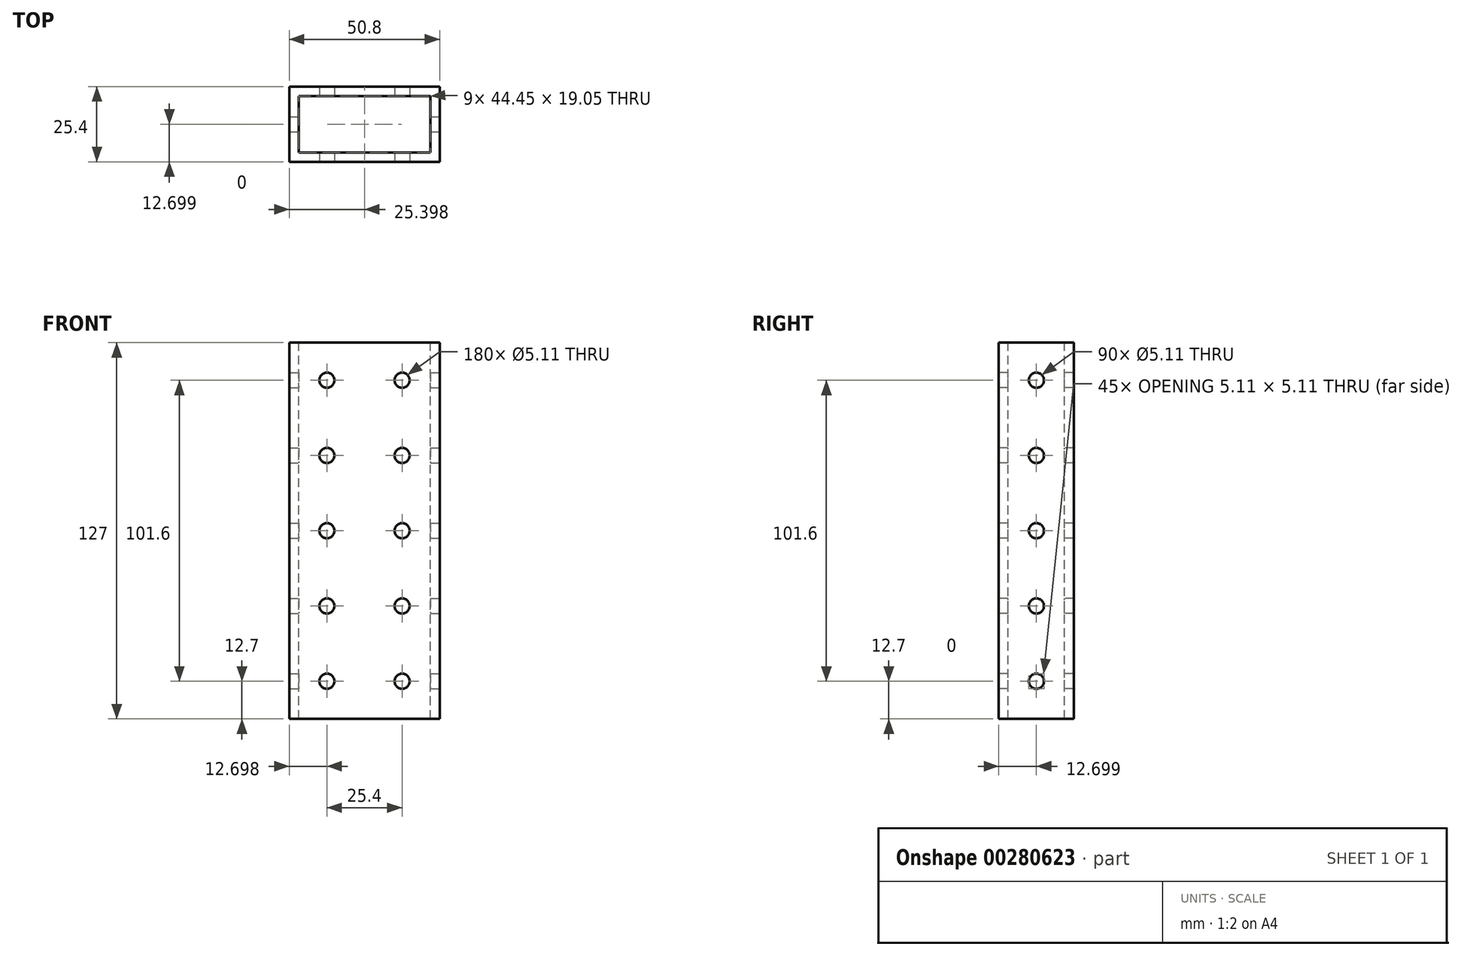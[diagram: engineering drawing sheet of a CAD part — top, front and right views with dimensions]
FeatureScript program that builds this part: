
annotation { "Feature Type Name" : "Feature", "Feature Type Description" : "" }
export const myFeature = defineFeature(function(context is Context, id is Id, definition is map)
    precondition{}
    {
        {
            var Q0;
            Q0=qCreatedBy(makeId("Top.planeOp"),FACE);
            var sketch = newSketch(context, id + "F0", { "sketchPlane" : qUnion([Q0])});
            skLineSegment(sketch, "E0.bottom", {"start": v(-19.05, 5.92) * mm, "end": v(31.75, 5.92) * mm});
            skLineSegment(sketch, "E0.top", {"start": v(-19.05, -19.48) * mm, "end": v(31.75, -19.48) * mm});
            skLineSegment(sketch, "E0.left", {"start": v(-19.05, 5.92) * mm, "end": v(-19.05, -19.48) * mm});
            skLineSegment(sketch, "E0.right", {"start": v(31.75, 5.92) * mm, "end": v(31.75, -19.48) * mm});
            skSolve(sketch);
        }
        {
            var Q0;
            Q0=qSketchRegion(id+"F0",true);
            extrude(context, id + "F1", {"entities" : qUnion([Q0]), "depth" : 127 * mm});
        }
        {
            var Q0;
            Q0=makeQuery(id+"F1.opExtrude","CAP_FACE",FACE,{"disambiguationData":[OSD([sQuery(id+"F0.wireOp",EDGE,"E0.bottom"),sQuery(id+"F0.wireOp",EDGE,"E0.top"),sQuery(id+"F0.wireOp",EDGE,"E0.left"),sQuery(id+"F0.wireOp",EDGE,"E0.right")])],"isStart":false});
            var sketch = newSketch(context, id + "F2", { "sketchPlane" : qUnion([Q0])});
            skLineSegment(sketch, "E1.bottom", {"start": v(-15.88, 2.74) * mm, "end": v(28.57, 2.74) * mm});
            skLineSegment(sketch, "E1.top", {"start": v(-15.88, -16.3) * mm, "end": v(28.57, -16.3) * mm});
            skLineSegment(sketch, "E1.left", {"start": v(-15.88, 2.74) * mm, "end": v(-15.88, -16.3) * mm});
            skLineSegment(sketch, "E1.right", {"start": v(28.57, 2.74) * mm, "end": v(28.57, -16.3) * mm});
            skSolve(sketch);
        }
        {
            var Q0;
            Q0=makeQuery(id+"F2.imprint","IMPRINT",FACE,{"disambiguationData":[TD([[makeQuery(id+"F2.imprint","IMPRINT",EDGE,{"derivedFrom":sQuery(id+"F2.wireOp",EDGE,"E1.bottom")}),-1.0]])]});
            extrude(context, id + "F3", {"entities" : qUnion([Q0]), "operationType" : NewBodyOperationType.REMOVE, "oppositeDirection" : true, "depth" : 127 * mm});
        }
        {
            var Q0;
            Q0=qCreatedBy(makeId("Right.planeOp"),FACE);
            var sketch = newSketch(context, id + "F4", { "sketchPlane" : qUnion([Q0])});
            skCircle(sketch, "E2", {"center": v(-6.78, 12.7) * mm, "radius": 2.55 * mm});
            skSolve(sketch);
        }
        {
            var Q0;
            Q0=sQuery(id+"F4.wireOp",VERTEX,"E2.center");
            var Q1;
            Q1=makeQuery(id+"F1.opExtrude","SWEPT_BODY",BODY,{"disambiguationData":[OSD([sQuery(id+"F0.wireOp",EDGE,"E0.bottom"),sQuery(id+"F0.wireOp",EDGE,"E0.top"),sQuery(id+"F0.wireOp",EDGE,"E0.left"),sQuery(id+"F0.wireOp",EDGE,"E0.right")])]});
            hole(context, id + "F5", {"style" : HoleStyle.SIMPLE, "endStyle" : HoleEndStyle.THROUGH, "holeDiameter" : 5.1 * mm, "tappedDepth" : 12.7 * mm, "tapClearance" : 3, "locations" : qUnion([Q0]), "scope" : qUnion([Q1])});
        }
        {
            var Q0;
            Q0=makeQuery(id+"F1.opExtrude","SWEPT_FACE",FACE,{"disambiguationData":[OSD([sQuery(id+"F0.wireOp",EDGE,"E0.right")])]});
            var sketch = newSketch(context, id + "F6", { "sketchPlane" : qUnion([Q0])});
            skCircle(sketch, "E3", {"center": v(-6.78, 114.3) * mm, "radius": 2.55 * mm});
            skCircle(sketch, "E4.0.1.0", {"center": v(-6.78, 88.9) * mm, "radius": 2.55 * mm});
            skCircle(sketch, "E4.0.2.0", {"center": v(-6.78, 63.5) * mm, "radius": 2.55 * mm});
            skCircle(sketch, "E4.0.3.0", {"center": v(-6.78, 38.1) * mm, "radius": 2.55 * mm});
            skCircle(sketch, "E4.0.4.0", {"center": v(-6.78, 12.7) * mm, "radius": 2.55 * mm});
            skLineSegment(sketch, "E4.direction1", {"start": v(-6.78, 114.3) * mm, "end": v(18.62, 114.3) * mm, "construction": true});
            skLineSegment(sketch, "E4.direction2", {"start": v(-6.78, 114.3) * mm, "end": v(-6.78, 88.9) * mm, "construction": true});
            skSolve(sketch);
        }
        {
            var Q0;
            Q0=sQuery(id+"F6.wireOp",VERTEX,"E4.0.1.0.center");
            var Q1;
            Q1=sQuery(id+"F6.wireOp",VERTEX,"E4.0.2.0.center");
            var Q2;
            Q2=sQuery(id+"F6.wireOp",VERTEX,"E4.direction1.start");
            var Q3;
            Q3=sQuery(id+"F6.wireOp",VERTEX,"E4.0.3.0.center");
            var Q4;
            Q4=sQuery(id+"F6.wireOp",VERTEX,"E4.0.4.0.center");
            var Q5;
            Q5=makeQuery(id+"F1.opExtrude","SWEPT_BODY",BODY,{"disambiguationData":[OSD([sQuery(id+"F0.wireOp",EDGE,"E0.bottom"),sQuery(id+"F0.wireOp",EDGE,"E0.top"),sQuery(id+"F0.wireOp",EDGE,"E0.left"),sQuery(id+"F0.wireOp",EDGE,"E0.right")])]});
            hole(context, id + "F7", {"style" : HoleStyle.SIMPLE, "endStyle" : HoleEndStyle.THROUGH, "holeDiameter" : 5.1 * mm, "tappedDepth" : 12.7 * mm, "tapClearance" : 3, "locations" : qUnion([Q0, Q1, Q2, Q3, Q4]), "scope" : qUnion([Q5])});
        }
        {
            var Q0;
            Q0=makeQuery(id+"F1.opExtrude","SWEPT_FACE",FACE,{"disambiguationData":[OSD([sQuery(id+"F0.wireOp",EDGE,"E0.top")])]});
            var sketch = newSketch(context, id + "F8", { "sketchPlane" : qUnion([Q0])});
            skCircle(sketch, "E5", {"center": v(-6.35, 114.3) * mm, "radius": 2.55 * mm});
            skCircle(sketch, "E6.0.1.0", {"center": v(-6.35, 88.9) * mm, "radius": 2.55 * mm});
            skCircle(sketch, "E6.0.2.0", {"center": v(-6.35, 63.5) * mm, "radius": 2.55 * mm});
            skCircle(sketch, "E6.0.3.0", {"center": v(-6.35, 38.1) * mm, "radius": 2.55 * mm});
            skCircle(sketch, "E6.0.4.0", {"center": v(-6.35, 12.7) * mm, "radius": 2.55 * mm});
            skLineSegment(sketch, "E6.direction1", {"start": v(-6.35, 114.3) * mm, "end": v(19.05, 114.3) * mm, "construction": true});
            skLineSegment(sketch, "E6.direction2", {"start": v(-6.35, 114.3) * mm, "end": v(-6.35, 88.9) * mm, "construction": true});
            skCircle(sketch, "E7.0.1.0", {"center": v(19.05, 114.3) * mm, "radius": 2.55 * mm});
            skCircle(sketch, "E7.0.1.1", {"center": v(19.05, 88.9) * mm, "radius": 2.55 * mm});
            skCircle(sketch, "E7.0.1.2", {"center": v(19.05, 63.5) * mm, "radius": 2.55 * mm});
            skCircle(sketch, "E7.0.1.3", {"center": v(19.05, 38.1) * mm, "radius": 2.55 * mm});
            skCircle(sketch, "E7.0.1.4", {"center": v(19.05, 12.7) * mm, "radius": 2.55 * mm});
            skSolve(sketch);
        }
        {
            var Q0;
            Q0=sQuery(id+"F8.wireOp",VERTEX,"E5.center");
            var Q1;
            Q1=sQuery(id+"F8.wireOp",VERTEX,"E6.0.1.0.center");
            var Q2;
            Q2=sQuery(id+"F8.wireOp",VERTEX,"E6.0.2.0.center");
            var Q3;
            Q3=sQuery(id+"F8.wireOp",VERTEX,"E6.0.3.0.center");
            var Q4;
            Q4=sQuery(id+"F8.wireOp",VERTEX,"E6.0.4.0.center");
            var Q5;
            Q5=sQuery(id+"F8.wireOp",VERTEX,"E7.0.1.2.center");
            var Q6;
            Q6=sQuery(id+"F8.wireOp",VERTEX,"E7.0.1.3.center");
            var Q7;
            Q7=sQuery(id+"F8.wireOp",VERTEX,"E7.0.1.1.center");
            var Q8;
            Q8=sQuery(id+"F8.wireOp",VERTEX,"E7.0.1.0.center");
            var Q9;
            Q9=sQuery(id+"F8.wireOp",VERTEX,"E7.0.1.4.center");
            var Q10;
            Q10=makeQuery(id+"F1.opExtrude","SWEPT_BODY",BODY,{"disambiguationData":[OSD([sQuery(id+"F0.wireOp",EDGE,"E0.bottom"),sQuery(id+"F0.wireOp",EDGE,"E0.top"),sQuery(id+"F0.wireOp",EDGE,"E0.left"),sQuery(id+"F0.wireOp",EDGE,"E0.right")])]});
            hole(context, id + "F9", {"style" : HoleStyle.SIMPLE, "endStyle" : HoleEndStyle.THROUGH, "holeDiameter" : 5.1 * mm, "tappedDepth" : 12.7 * mm, "tapClearance" : 3, "locations" : qUnion([Q0, Q1, Q2, Q3, Q4, Q5, Q6, Q7, Q8, Q9]), "scope" : qUnion([Q10])});
        }
    });
